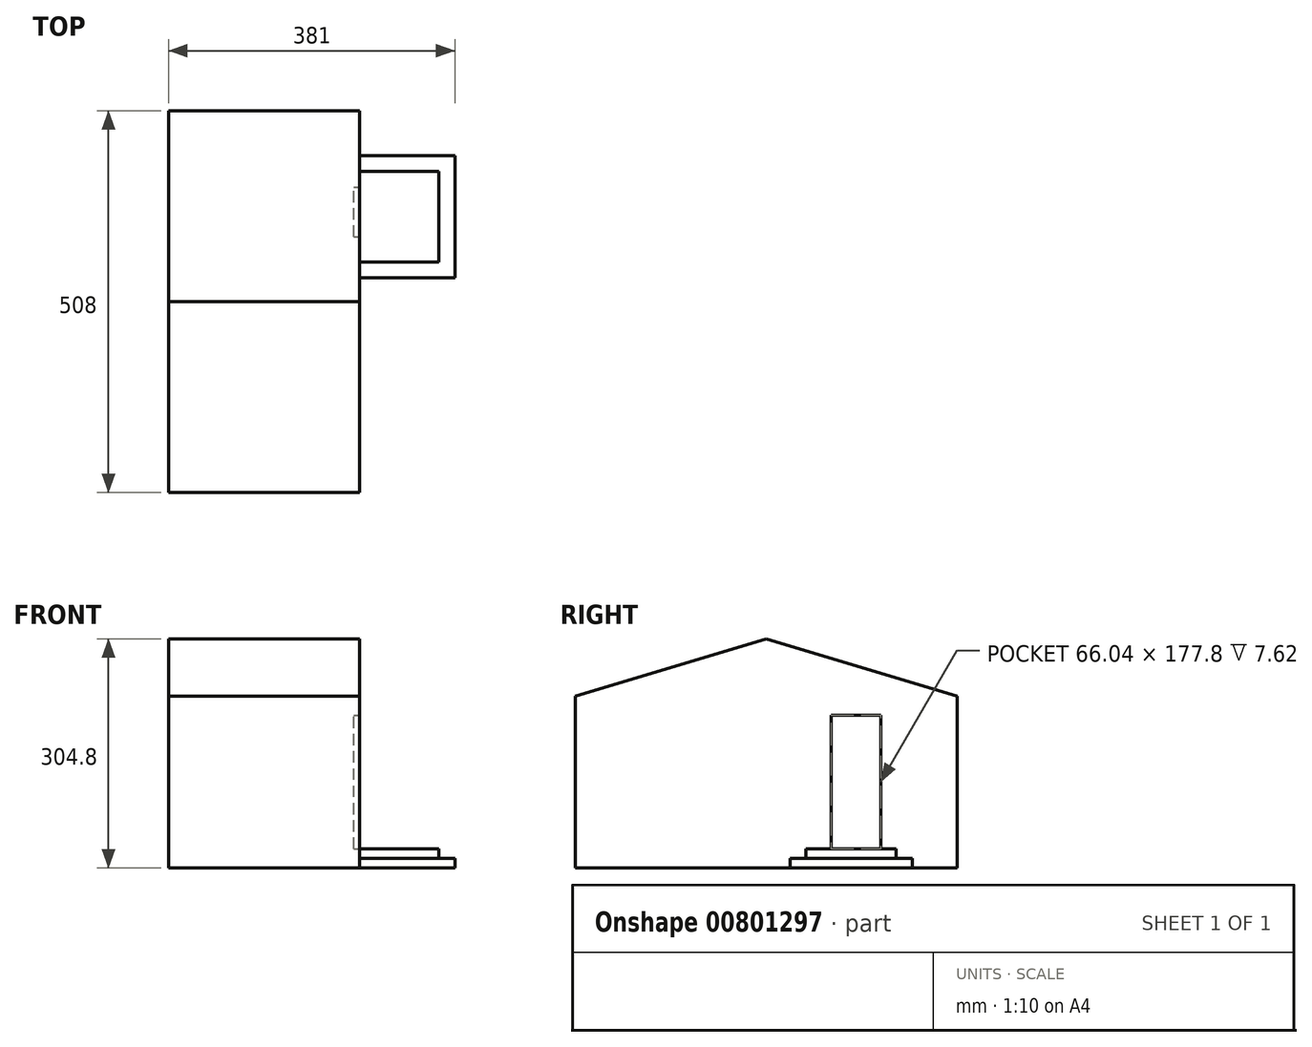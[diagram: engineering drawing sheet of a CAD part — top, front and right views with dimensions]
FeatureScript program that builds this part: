
annotation { "Feature Type Name" : "Feature", "Feature Type Description" : "" }
export const myFeature = defineFeature(function(context is Context, id is Id, definition is map)
    precondition{}
    {
        {
            var Q0;
            Q0=qCreatedBy(makeId("Right.planeOp"),FACE);
            var sketch = newSketch(context, id + "F0", { "sketchPlane" : qUnion([Q0])});
            skLineSegment(sketch, "E0", {"start": v(0, 0) * mm, "end": v(0, 228.6) * mm});
            skLineSegment(sketch, "E1", {"start": v(0, 228.6) * mm, "end": v(254, 304.8) * mm});
            skLineSegment(sketch, "E2", {"start": v(254, 304.8) * mm, "end": v(508, 228.6) * mm});
            skLineSegment(sketch, "E3", {"start": v(508, 228.6) * mm, "end": v(508, 0) * mm});
            skLineSegment(sketch, "E4", {"start": v(508, 0) * mm, "end": v(0, 0) * mm});
            skSolve(sketch);
        }
        {
            var Q0;
            Q0=qCreatedBy(makeId("Right.planeOp"),FACE);
            var sketch = newSketch(context, id + "F1", { "sketchPlane" : qUnion([Q0])});
            skLineSegment(sketch, "E5.bottom", {"start": v(340.36, 25.4) * mm, "end": v(406.4, 25.4) * mm});
            skLineSegment(sketch, "E5.top", {"start": v(340.36, 203.2) * mm, "end": v(406.4, 203.2) * mm});
            skLineSegment(sketch, "E5.left", {"start": v(340.36, 25.4) * mm, "end": v(340.36, 203.2) * mm});
            skLineSegment(sketch, "E5.right", {"start": v(406.4, 25.4) * mm, "end": v(406.4, 203.2) * mm});
            skSolve(sketch);
        }
        {
            var Q0;
            Q0=qCreatedBy(makeId("Top.planeOp"),FACE);
            var sketch = newSketch(context, id + "F2", { "sketchPlane" : qUnion([Q0])});
            skLineSegment(sketch, "E6.bottom", {"start": v(0, 448.23) * mm, "end": v(127, 448.23) * mm});
            skLineSegment(sketch, "E6.top", {"start": v(0, 285.66) * mm, "end": v(127, 285.66) * mm});
            skLineSegment(sketch, "E6.left", {"start": v(0, 448.23) * mm, "end": v(0, 285.66) * mm});
            skLineSegment(sketch, "E6.right", {"start": v(127, 448.23) * mm, "end": v(127, 285.66) * mm});
            skSolve(sketch);
        }
        {
            var Q0;
            Q0=makeQuery(id+"F2.imprint","IMPRINT",FACE,{"disambiguationData":[TD([[makeQuery(id+"F2.imprint","IMPRINT",EDGE,{"derivedFrom":sQuery(id+"F2.wireOp",EDGE,"E6.bottom")}),-1.0]])]});
            extrude(context, id + "F3", {"entities" : qUnion([Q0]), "depth" : 12.7 * mm, "offsetDistance" : 25.4 * mm});
        }
        {
            var Q0;
            Q0=makeQuery(id+"F3.opExtrude","CAP_FACE",FACE,{"disambiguationData":[OSD([sQuery(id+"F2.wireOp",EDGE,"E6.bottom"),sQuery(id+"F2.wireOp",EDGE,"E6.top"),sQuery(id+"F2.wireOp",EDGE,"E6.left"),sQuery(id+"F2.wireOp",EDGE,"E6.right")])],"isStart":false});
            var sketch = newSketch(context, id + "F4", { "sketchPlane" : qUnion([Q0])});
            skLineSegment(sketch, "E7.bottom", {"start": v(0, 427.07) * mm, "end": v(105.83, 427.07) * mm});
            skLineSegment(sketch, "E7.top", {"start": v(0, 306.82) * mm, "end": v(105.83, 306.82) * mm});
            skLineSegment(sketch, "E7.left", {"start": v(0, 427.07) * mm, "end": v(0, 306.82) * mm});
            skLineSegment(sketch, "E7.right", {"start": v(105.83, 427.07) * mm, "end": v(105.83, 306.82) * mm});
            skSolve(sketch);
        }
        {
            var Q0;
            Q0=makeQuery(id+"F4.imprint","IMPRINT",FACE,{"disambiguationData":[TD([[makeQuery(id+"F4.imprint","IMPRINT",EDGE,{"derivedFrom":sQuery(id+"F4.wireOp",EDGE,"E7.bottom")}),-1.0]])]});
            extrude(context, id + "F5", {"entities" : qUnion([Q0]), "operationType" : NewBodyOperationType.ADD, "depth" : 12.7 * mm, "offsetDistance" : 25.4 * mm});
        }
        {
            var Q0;
            Q0=makeQuery(id+"F0.imprint","IMPRINT",FACE,{"disambiguationData":[TD([[makeQuery(id+"F0.imprint","IMPRINT",EDGE,{"derivedFrom":sQuery(id+"F0.wireOp",EDGE,"E0")}),-1.0]])]});
            extrude(context, id + "F6", {"entities" : qUnion([Q0]), "operationType" : NewBodyOperationType.ADD, "oppositeDirection" : true, "depth" : 254 * mm, "offsetDistance" : 25.4 * mm});
        }
        {
            var Q0;
            Q0=makeQuery(id+"F1.imprint","IMPRINT",FACE,{"disambiguationData":[TD([[makeQuery(id+"F1.imprint","IMPRINT",EDGE,{"derivedFrom":sQuery(id+"F1.wireOp",EDGE,"E5.bottom")}),1.0]])]});
            extrude(context, id + "F7", {"entities" : qUnion([Q0]), "operationType" : NewBodyOperationType.REMOVE, "oppositeDirection" : true, "depth" : 7.62 * mm, "offsetDistance" : 25.4 * mm});
        }
    });
